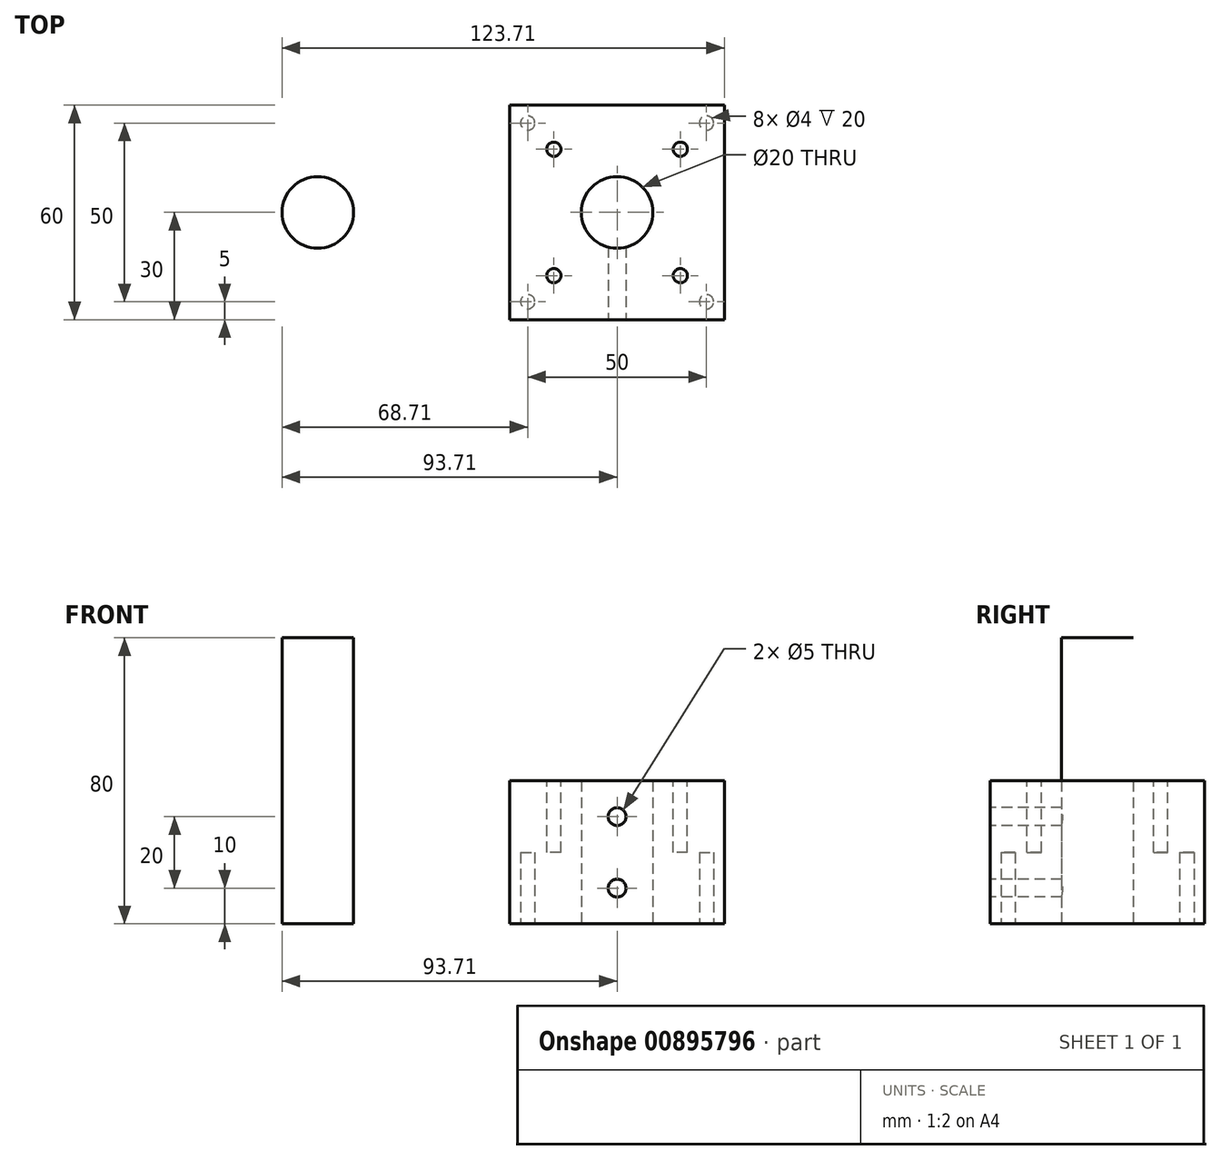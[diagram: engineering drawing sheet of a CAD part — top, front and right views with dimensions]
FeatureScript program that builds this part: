
annotation { "Feature Type Name" : "Feature", "Feature Type Description" : "" }
export const myFeature = defineFeature(function(context is Context, id is Id, definition is map)
    precondition{}
    {
        {
            var Q0;
            Q0=qCreatedBy(makeId("Top.planeOp"),FACE);
            var sketch = newSketch(context, id + "F0", { "sketchPlane" : qUnion([Q0])});
            skLineSegment(sketch, "E0.bottom", {"start": v(-30, 30) * mm, "end": v(30, 30) * mm});
            skLineSegment(sketch, "E0.top", {"start": v(-30, -30) * mm, "end": v(30, -30) * mm});
            skLineSegment(sketch, "E0.left", {"start": v(-30, 30) * mm, "end": v(-30, -30) * mm});
            skLineSegment(sketch, "E0.right", {"start": v(30, 30) * mm, "end": v(30, -30) * mm});
            skPoint(sketch, "E0.middle", {"position": v(0, 0) * mm});
            skCircle(sketch, "E1", {"center": v(0, 0) * mm, "radius": 10 * mm});
            skCircle(sketch, "E2", {"center": v(-83.7, 0) * mm, "radius": 10 * mm});
            skSolve(sketch);
        }
        {
            var Q0;
            Q0=makeQuery(id+"F0.imprint","IMPRINT",FACE,{"disambiguationData":[TD([[makeQuery(id+"F0.imprint","IMPRINT",EDGE,{"derivedFrom":sQuery(id+"F0.wireOp",EDGE,"E0.bottom")}),-1.0]])]});
            extrude(context, id + "F1", {"entities" : qUnion([Q0]), "depth" : 40 * mm, "offsetDistance" : 25 * mm});
        }
        {
            var Q0;
            Q0=makeQuery(id+"F1.opExtrude","CAP_FACE",FACE,{"disambiguationData":[OSD([sQuery(id+"F0.wireOp",EDGE,"E0.bottom"),sQuery(id+"F0.wireOp",EDGE,"E0.top"),sQuery(id+"F0.wireOp",EDGE,"E0.left"),sQuery(id+"F0.wireOp",EDGE,"E0.right"),sQuery(id+"F0.wireOp",EDGE,"E1")])],"isStart":true});
            var sketch = newSketch(context, id + "F2", { "sketchPlane" : qUnion([Q0])});
            skCircle(sketch, "E3", {"center": v(-25, 25) * mm, "radius": 2 * mm});
            skCircle(sketch, "E4", {"center": v(25, 25) * mm, "radius": 2 * mm});
            skCircle(sketch, "E5.MirrorC", {"center": v(-25, -25) * mm, "radius": 2 * mm});
            skCircle(sketch, "E6.MirrorC", {"center": v(25, -25) * mm, "radius": 2 * mm});
            skSolve(sketch);
        }
        {
            var Q0;
            Q0 = qSketchRegion(id + "F2", true);
            extrude(context, id + "F3", {"entities" : qUnion([Q0]), "operationType" : NewBodyOperationType.REMOVE, "oppositeDirection" : true, "depth" : 20 * mm, "offsetDistance" : 25 * mm});
        }
        {
            var Q0;
            Q0=makeQuery(id+"F1.opExtrude","SWEPT_FACE",FACE,{"disambiguationData":[OSD([sQuery(id+"F0.wireOp",EDGE,"E0.top")])]});
            var sketch = newSketch(context, id + "F4", { "sketchPlane" : qUnion([Q0])});
            skCircle(sketch, "E7", {"center": v(0, 30) * mm, "radius": 2.5 * mm});
            skCircle(sketch, "E8", {"center": v(0, 10) * mm, "radius": 2.5 * mm});
            skSolve(sketch);
        }
        {
            var Q0;
            Q0 = qSketchRegion(id + "F4", true);
            extrude(context, id + "F5", {"entities" : qUnion([Q0]), "operationType" : NewBodyOperationType.REMOVE, "oppositeDirection" : true, "depth" : 25 * mm, "offsetDistance" : 25 * mm});
        }
        {
            var Q0;
            Q0=makeQuery(id+"F0.imprint","IMPRINT",FACE,{"disambiguationData":[TD([[makeQuery(id+"F0.imprint","IMPRINT",EDGE,{"derivedFrom":sQuery(id+"F0.wireOp",EDGE,"E2")}),1.0]])]});
            extrude(context, id + "F6", {"entities" : qUnion([Q0]), "depth" : 80 * mm, "offsetDistance" : 25 * mm});
        }
        {
            var Q0;
            Q0=makeQuery(id+"F1.opExtrude","CAP_FACE",FACE,{"disambiguationData":[OSD([sQuery(id+"F0.wireOp",EDGE,"E0.bottom"),sQuery(id+"F0.wireOp",EDGE,"E0.top"),sQuery(id+"F0.wireOp",EDGE,"E0.left"),sQuery(id+"F0.wireOp",EDGE,"E0.right"),sQuery(id+"F0.wireOp",EDGE,"E1")])],"isStart":false});
            var sketch = newSketch(context, id + "F7", { "sketchPlane" : qUnion([Q0])});
            skCircle(sketch, "E9.1.0", {"center": v(-17.68, 17.68) * mm, "radius": 2 * mm});
            skCircle(sketch, "E9.3.0", {"center": v(-17.68, -17.68) * mm, "radius": 2 * mm});
            skCircle(sketch, "E9.5.0", {"center": v(17.68, -17.68) * mm, "radius": 2 * mm});
            skCircle(sketch, "E9.7.0", {"center": v(17.68, 17.68) * mm, "radius": 2 * mm});
            skPoint(sketch, "E9.center", {"position": v(0, 0) * mm});
            skSolve(sketch);
        }
        {
            var Q0;
            Q0 = qSketchRegion(id + "F7", true);
            extrude(context, id + "F8", {"entities" : qUnion([Q0]), "operationType" : NewBodyOperationType.REMOVE, "oppositeDirection" : true, "depth" : 20 * mm, "offsetDistance" : 25 * mm});
        }
    });
